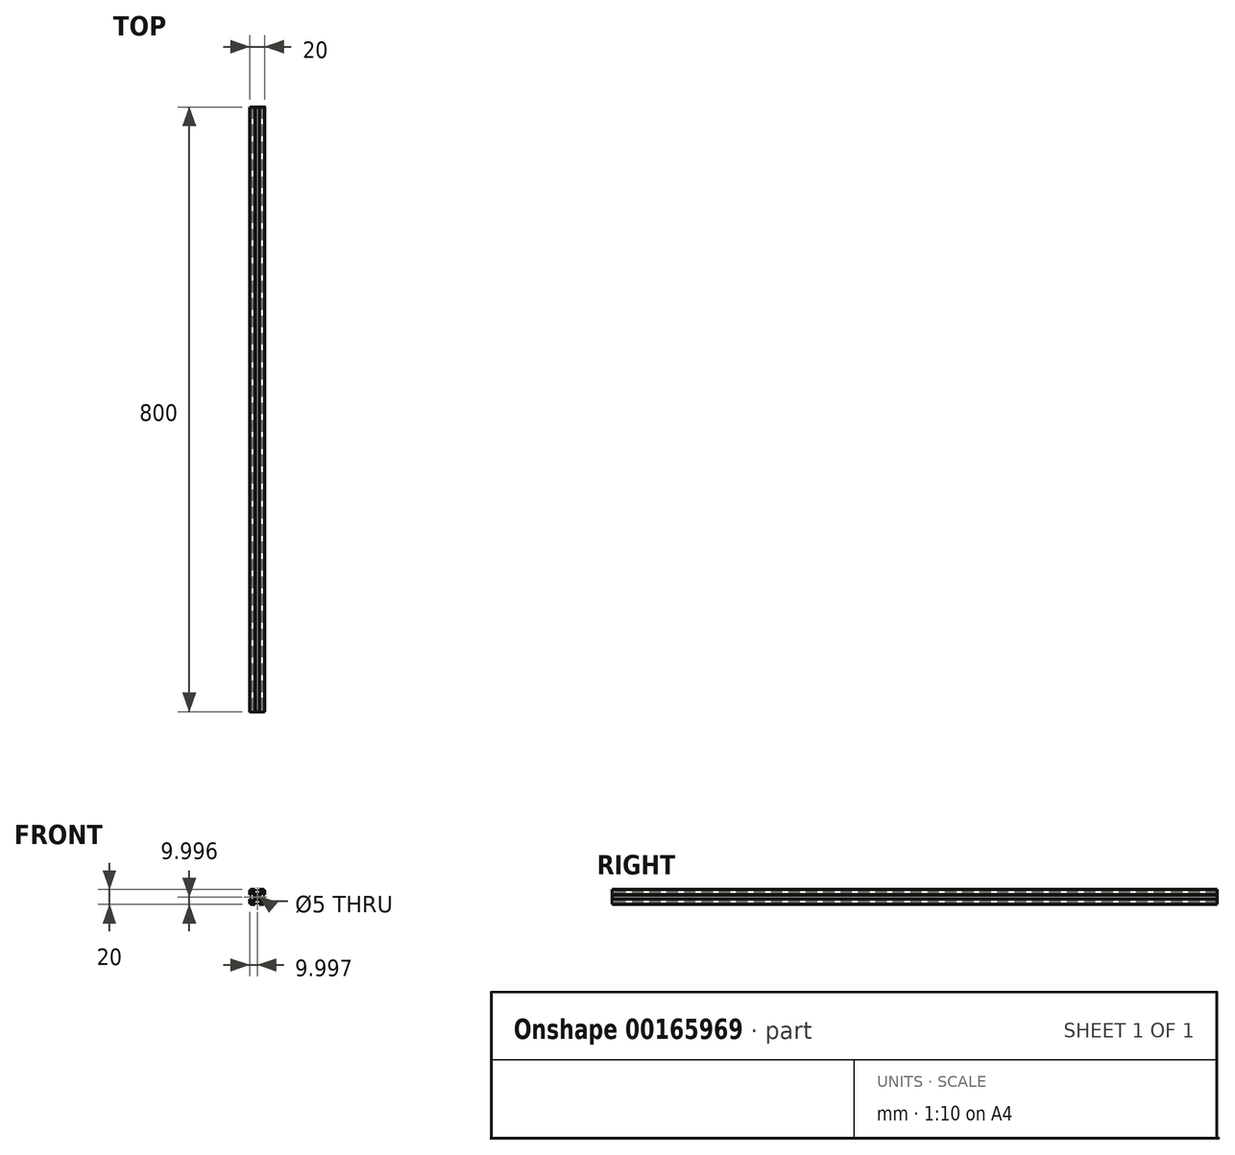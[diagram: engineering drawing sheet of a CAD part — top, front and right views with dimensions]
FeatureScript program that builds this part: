
annotation { "Feature Type Name" : "Feature", "Feature Type Description" : "" }
export const myFeature = defineFeature(function(context is Context, id is Id, definition is map)
    precondition{}
    {
        {
            var Q0;
            Q0=qCreatedBy(makeId("Front.planeOp"),FACE);
            var sketch = newSketch(context, id + "F0", { "sketchPlane" : qUnion([Q0])});
            skCircle(sketch, "E0", {"center": v(0.09, 0.12) * mm, "radius": 2.5 * mm});
            skLineSegment(sketch, "E1.bottom", {"start": v(7.09, -9.88) * mm, "end": v(3.09, -9.88) * mm});
            skLineSegment(sketch, "E1.top", {"start": v(7.09, 10.12) * mm, "end": v(3.09, 10.12) * mm});
            skLineSegment(sketch, "E1.left", {"start": v(10.09, -6.88) * mm, "end": v(10.09, -2.88) * mm});
            skLineSegment(sketch, "E1.right", {"start": v(-9.91, -6.88) * mm, "end": v(-9.91, -2.88) * mm});
            skLineSegment(sketch, "E2.bottom", {"start": v(2.63, -3.48) * mm, "end": v(-2.45, -3.48) * mm});
            skLineSegment(sketch, "E2.top", {"start": v(2.63, 3.72) * mm, "end": v(-2.45, 3.72) * mm});
            skLineSegment(sketch, "E2.left", {"start": v(3.69, -2.42) * mm, "end": v(3.69, 2.65) * mm});
            skLineSegment(sketch, "E2.right", {"start": v(-3.51, -2.42) * mm, "end": v(-3.51, 2.65) * mm});
            skLineSegment(sketch, "E3.bottom", {"start": v(7.03, -7.88) * mm, "end": v(3.09, -7.88) * mm});
            skLineSegment(sketch, "E3.top", {"start": v(7.03, 8.12) * mm, "end": v(3.09, 8.12) * mm});
            skLineSegment(sketch, "E3.left", {"start": v(8.09, -6.82) * mm, "end": v(8.09, -2.88) * mm});
            skLineSegment(sketch, "E3.right", {"start": v(-7.91, -6.82) * mm, "end": v(-7.91, -2.88) * mm});
            skLineSegment(sketch, "E4", {"start": v(-7.91, 8.12) * mm, "end": v(8.09, -7.88) * mm, "construction": true});
            skLineSegment(sketch, "E5", {"start": v(-7.91, -7.88) * mm, "end": v(8.09, 8.12) * mm, "construction": true});
            skLineSegment(sketch, "E6", {"start": v(-6.85, 8.12) * mm, "end": v(-2.45, 3.72) * mm});
            skLineSegment(sketch, "E7", {"start": v(-7.91, 7.05) * mm, "end": v(-3.51, 2.65) * mm});
            skLineSegment(sketch, "E8", {"start": v(7.03, 8.12) * mm, "end": v(2.63, 3.72) * mm});
            skLineSegment(sketch, "E9", {"start": v(8.09, 7.05) * mm, "end": v(3.69, 2.65) * mm});
            skLineSegment(sketch, "E10.trimOffspring", {"start": v(3.69, -2.42) * mm, "end": v(8.09, -6.82) * mm});
            skLineSegment(sketch, "E11.trimOffspring", {"start": v(2.63, -3.48) * mm, "end": v(7.03, -7.88) * mm});
            skLineSegment(sketch, "E12.trimOffspring", {"start": v(-2.45, -3.48) * mm, "end": v(-6.85, -7.88) * mm});
            skLineSegment(sketch, "E13.trimOffspring", {"start": v(-3.51, -2.42) * mm, "end": v(-7.91, -6.82) * mm});
            skPoint(sketch, "E14.orphan", {"position": v(3.69, 3.72) * mm});
            skPoint(sketch, "E15.orphan", {"position": v(-3.51, 3.72) * mm});
            skPoint(sketch, "E16.orphan", {"position": v(3.69, -3.48) * mm});
            skPoint(sketch, "E17.orphan", {"position": v(-3.51, -3.48) * mm});
            skLineSegment(sketch, "E18", {"start": v(-9.91, 3.12) * mm, "end": v(-7.91, 3.12) * mm});
            skLineSegment(sketch, "E19.MirrorCS", {"start": v(-9.91, -2.88) * mm, "end": v(-7.91, -2.88) * mm});
            skLineSegment(sketch, "E20.MirrorCS", {"start": v(10.09, 3.12) * mm, "end": v(8.09, 3.12) * mm});
            skLineSegment(sketch, "E21.MirrorCS", {"start": v(10.09, -2.88) * mm, "end": v(8.09, -2.88) * mm});
            skLineSegment(sketch, "E22", {"start": v(-2.91, 10.12) * mm, "end": v(-2.91, 8.12) * mm});
            skLineSegment(sketch, "E23.MirrorCS", {"start": v(3.09, 10.12) * mm, "end": v(3.09, 8.12) * mm});
            skLineSegment(sketch, "E24.MirrorCS", {"start": v(3.09, -9.88) * mm, "end": v(3.09, -7.88) * mm});
            skLineSegment(sketch, "E25.MirrorCS", {"start": v(-2.91, -9.88) * mm, "end": v(-2.91, -7.88) * mm});
            skLineSegment(sketch, "E26.trimOffspring", {"start": v(-2.91, 10.12) * mm, "end": v(-6.91, 10.12) * mm});
            skLineSegment(sketch, "E27.trimOffspring", {"start": v(-2.91, 8.12) * mm, "end": v(-6.85, 8.12) * mm});
            skLineSegment(sketch, "E28.trimOffspring", {"start": v(-2.91, -7.88) * mm, "end": v(-6.85, -7.88) * mm});
            skLineSegment(sketch, "E29.trimOffspring", {"start": v(-2.91, -9.88) * mm, "end": v(-6.91, -9.88) * mm});
            skLineSegment(sketch, "E30.trimOffspring", {"start": v(10.09, 3.12) * mm, "end": v(10.09, 7.12) * mm});
            skLineSegment(sketch, "E31.trimOffspring", {"start": v(8.09, 3.12) * mm, "end": v(8.09, 7.05) * mm});
            skLineSegment(sketch, "E32.trimOffspring", {"start": v(-7.91, 3.12) * mm, "end": v(-7.91, 7.05) * mm});
            skLineSegment(sketch, "E33.trimOffspring", {"start": v(-9.91, 3.12) * mm, "end": v(-9.91, 7.12) * mm});
            skPoint(sketch, "E34.visualSharp", {"position": v(-9.91, 10.12) * mm});
            skArc(sketch, "E34.filletArc", {"start": v(-6.91, 10.12) * mm, "mid": v(-9.03, 9.24) * mm, "end": v(-9.91, 7.12) * mm});
            skPoint(sketch, "E35.visualSharp", {"position": v(10.09, 10.12) * mm});
            skArc(sketch, "E35.filletArc", {"start": v(10.09, 7.12) * mm, "mid": v(9.2, 9.24) * mm, "end": v(7.09, 10.12) * mm});
            skPoint(sketch, "E36.visualSharp", {"position": v(10.09, -9.88) * mm});
            skArc(sketch, "E36.filletArc", {"start": v(7.09, -9.88) * mm, "mid": v(9.2, -9) * mm, "end": v(10.09, -6.88) * mm});
            skPoint(sketch, "E37.visualSharp", {"position": v(-9.91, -9.88) * mm});
            skArc(sketch, "E37.filletArc", {"start": v(-9.91, -6.88) * mm, "mid": v(-9.03, -9) * mm, "end": v(-6.91, -9.88) * mm});
            skLineSegment(sketch, "E38", {"start": v(-5.41, 8.12) * mm, "end": v(-5.41, 6.68) * mm});
            skLineSegment(sketch, "E39", {"start": v(-7.91, 5.62) * mm, "end": v(-6.47, 5.62) * mm});
            skLineSegment(sketch, "E40.MirrorCS", {"start": v(5.59, 8.12) * mm, "end": v(5.59, 6.68) * mm});
            skLineSegment(sketch, "E41.MirrorCS", {"start": v(-5.41, -7.88) * mm, "end": v(-5.41, -6.45) * mm});
            skLineSegment(sketch, "E42.MirrorCS", {"start": v(-7.91, -5.38) * mm, "end": v(-6.47, -5.38) * mm});
            skLineSegment(sketch, "E43.MirrorCS", {"start": v(5.59, -7.88) * mm, "end": v(5.59, -6.45) * mm});
            skLineSegment(sketch, "E44.MirrorCS", {"start": v(8.09, 5.62) * mm, "end": v(6.65, 5.62) * mm});
            skLineSegment(sketch, "E45.MirrorCS", {"start": v(8.09, -5.38) * mm, "end": v(6.65, -5.38) * mm});
            skSolve(sketch);
        }
        {
            var Q0;
            Q0 = qSketchRegion(id + "F0", true);
            extrude(context, id + "F1", {"entities" : qUnion([Q0]), "oppositeDirection" : true, "depth" : 800 * mm});
        }
    });
